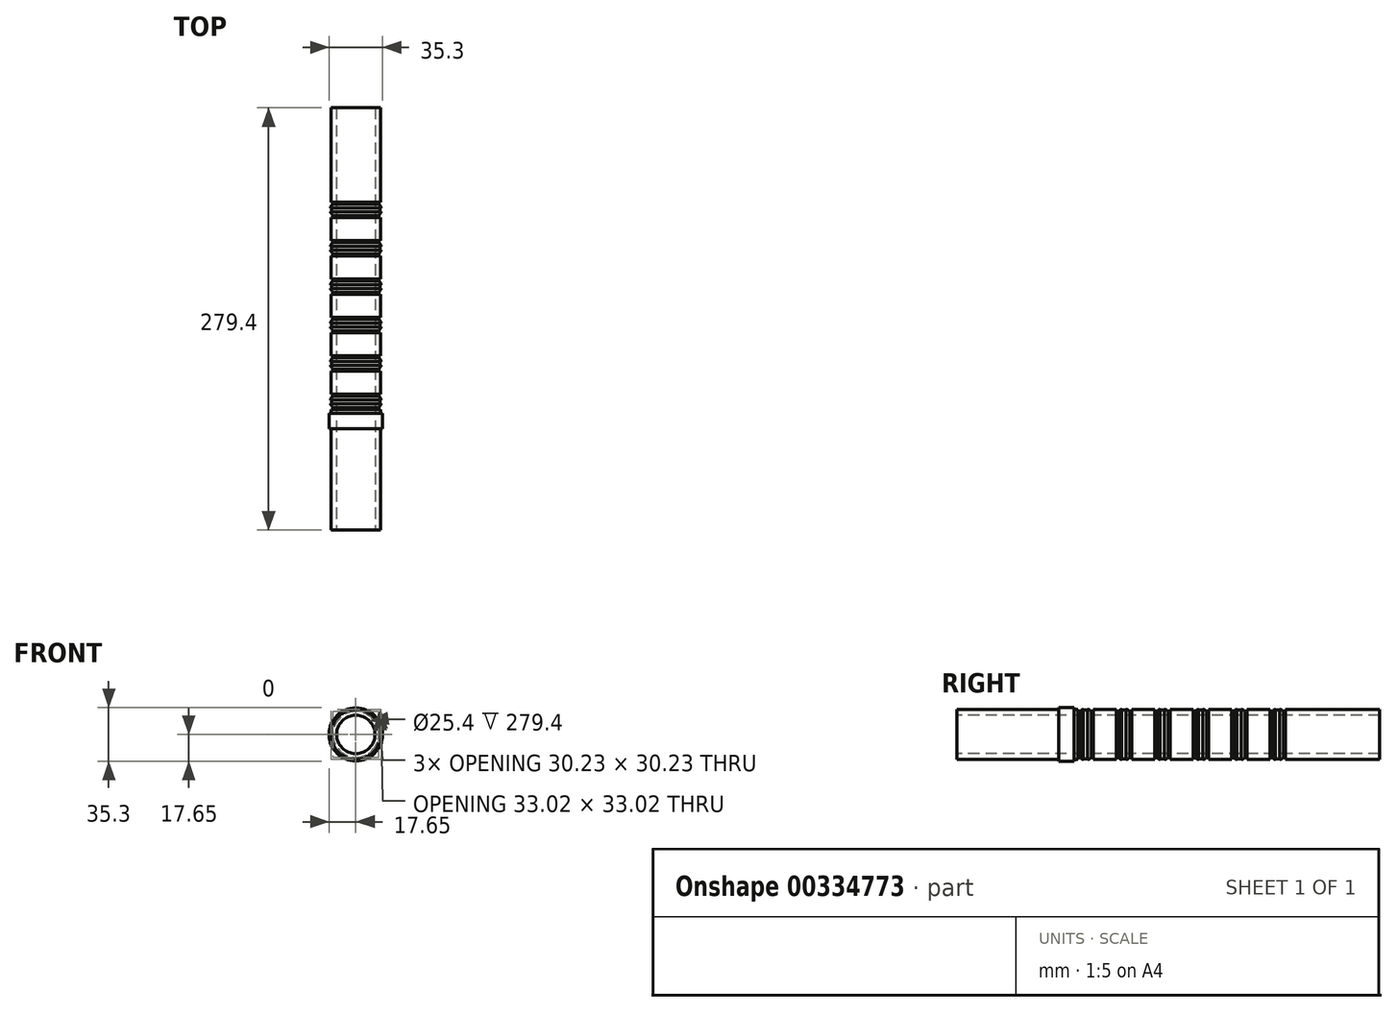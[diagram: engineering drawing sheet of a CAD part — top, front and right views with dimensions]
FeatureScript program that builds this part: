
annotation { "Feature Type Name" : "Feature", "Feature Type Description" : "" }
export const myFeature = defineFeature(function(context is Context, id is Id, definition is map)
    precondition{}
    {
        {
            var Q0;
            Q0=qCreatedBy(makeId("Front.planeOp"),FACE);
            var sketch = newSketch(context, id + "F0", { "sketchPlane" : qUnion([Q0])});
            skCircle(sketch, "E0", {"center": v(0, 0) * mm, "radius": 12.7 * mm});
            skCircle(sketch, "E1", {"center": v(0, 0) * mm, "radius": 16.51 * mm});
            skSolve(sketch);
        }
        {
            var Q0;
            Q0=makeQuery(id+"F0.imprint","IMPRINT",FACE,{"disambiguationData":[TD([[makeQuery(id+"F0.imprint","IMPRINT",EDGE,{"derivedFrom":sQuery(id+"F0.wireOp",EDGE,"E0")}),-1.0]])]});
            extrude(context, id + "F1", {"entities" : qUnion([Q0]), "oppositeDirection" : true, "depth" : 139.7 * mm, "hasSecondDirection" : true, "secondDirectionOppositeDirection" : false, "secondDirectionDepth" : 139.7 * mm});
        }
        {
            var Q0;
            Q0=qCreatedBy(makeId("Right.planeOp"),FACE);
            var sketch = newSketch(context, id + "F2", { "sketchPlane" : qUnion([Q0])});
            skLineSegment(sketch, "E2.bottom", {"start": v(-72.5, 17.65) * mm, "end": v(-62.33, 17.65) * mm});
            skLineSegment(sketch, "E2.top", {"start": v(-72.5, 15.11) * mm, "end": v(-62.33, 15.11) * mm});
            skLineSegment(sketch, "E2.left", {"start": v(-72.5, 17.65) * mm, "end": v(-72.5, 15.11) * mm});
            skLineSegment(sketch, "E2.right", {"start": v(-62.33, 17.65) * mm, "end": v(-62.33, 15.11) * mm});
            skLineSegment(sketch, "E3.1.0.0", {"start": v(-47.1, 17.65) * mm, "end": v(-36.93, 17.65) * mm});
            skLineSegment(sketch, "E3.1.0.1", {"start": v(-36.93, 17.65) * mm, "end": v(-36.93, 15.11) * mm});
            skLineSegment(sketch, "E3.1.0.2", {"start": v(-47.1, 15.11) * mm, "end": v(-36.93, 15.11) * mm});
            skLineSegment(sketch, "E3.1.0.3", {"start": v(-47.1, 17.65) * mm, "end": v(-47.1, 15.11) * mm});
            skLineSegment(sketch, "E3.2.0.0", {"start": v(-21.7, 17.65) * mm, "end": v(-11.53, 17.65) * mm});
            skLineSegment(sketch, "E3.2.0.1", {"start": v(-11.53, 17.65) * mm, "end": v(-11.53, 15.11) * mm});
            skLineSegment(sketch, "E3.2.0.2", {"start": v(-21.7, 15.11) * mm, "end": v(-11.53, 15.11) * mm});
            skLineSegment(sketch, "E3.2.0.3", {"start": v(-21.7, 17.65) * mm, "end": v(-21.7, 15.11) * mm});
            skLineSegment(sketch, "E4.1.0.0", {"start": v(3.7, 15.11) * mm, "end": v(13.87, 15.11) * mm});
            skLineSegment(sketch, "E4.1.0.1", {"start": v(13.87, 17.65) * mm, "end": v(13.87, 15.11) * mm});
            skLineSegment(sketch, "E4.1.0.2", {"start": v(3.7, 17.65) * mm, "end": v(3.7, 15.11) * mm});
            skLineSegment(sketch, "E4.1.0.4", {"start": v(29.1, 17.65) * mm, "end": v(39.27, 17.65) * mm});
            skLineSegment(sketch, "E4.1.0.5", {"start": v(29.1, 17.65) * mm, "end": v(29.1, 15.11) * mm});
            skLineSegment(sketch, "E4.1.0.6", {"start": v(29.1, 15.11) * mm, "end": v(39.27, 15.11) * mm});
            skLineSegment(sketch, "E4.1.0.7", {"start": v(39.27, 17.65) * mm, "end": v(39.27, 15.11) * mm});
            skLineSegment(sketch, "E4.1.0.8", {"start": v(54.5, 17.65) * mm, "end": v(54.5, 15.11) * mm});
            skLineSegment(sketch, "E4.1.0.9", {"start": v(54.5, 17.65) * mm, "end": v(64.67, 17.65) * mm});
            skLineSegment(sketch, "E4.1.0.10", {"start": v(54.5, 15.11) * mm, "end": v(64.67, 15.11) * mm});
            skLineSegment(sketch, "E4.1.0.11", {"start": v(64.67, 17.65) * mm, "end": v(64.67, 15.11) * mm});
            skLineSegment(sketch, "E4.2.0.0", {"start": v(79.9, 15.11) * mm, "end": v(90.07, 15.11) * mm});
            skLineSegment(sketch, "E4.2.0.1", {"start": v(90.07, 17.65) * mm, "end": v(90.07, 15.11) * mm});
            skLineSegment(sketch, "E4.2.0.2", {"start": v(79.9, 17.65) * mm, "end": v(79.9, 15.11) * mm});
            skLineSegment(sketch, "E5.trimOffspring", {"start": v(-21.7, 15.11) * mm, "end": v(-11.53, 15.11) * mm, "construction": true});
            skLineSegment(sketch, "E6.trimOffspring", {"start": v(-47.1, 15.11) * mm, "end": v(-36.93, 15.11) * mm, "construction": true});
            skLineSegment(sketch, "E7", {"start": v(3.7, 17.65) * mm, "end": v(13.87, 17.65) * mm});
            skLineSegment(sketch, "E8", {"start": v(79.9, 17.65) * mm, "end": v(90.07, 17.65) * mm});
            skLineSegment(sketch, "E9", {"start": v(-145.94, 0) * mm, "end": v(157.27, 0) * mm});
            skLineSegment(sketch, "E10.1.0.0", {"start": v(-49.63, 17.65) * mm, "end": v(-49.63, 15.11) * mm});
            skLineSegment(sketch, "E10.1.0.1", {"start": v(-59.8, 17.65) * mm, "end": v(-49.63, 17.65) * mm});
            skLineSegment(sketch, "E10.1.0.2", {"start": v(-59.8, 15.11) * mm, "end": v(-49.63, 15.11) * mm});
            skLineSegment(sketch, "E10.1.0.3", {"start": v(-59.8, 17.65) * mm, "end": v(-59.8, 15.11) * mm});
            skLineSegment(sketch, "E10.3.0.0", {"start": v(-24.23, 17.65) * mm, "end": v(-24.23, 15.11) * mm});
            skLineSegment(sketch, "E10.3.0.1", {"start": v(-34.4, 17.65) * mm, "end": v(-24.23, 17.65) * mm});
            skLineSegment(sketch, "E10.3.0.2", {"start": v(-34.4, 15.11) * mm, "end": v(-24.23, 15.11) * mm});
            skLineSegment(sketch, "E10.3.0.3", {"start": v(-34.4, 17.65) * mm, "end": v(-34.4, 15.11) * mm});
            skLineSegment(sketch, "E10.5.0.0", {"start": v(1.17, 17.65) * mm, "end": v(1.17, 15.11) * mm});
            skLineSegment(sketch, "E10.5.0.1", {"start": v(-9, 17.65) * mm, "end": v(1.17, 17.65) * mm});
            skLineSegment(sketch, "E10.5.0.2", {"start": v(-9, 15.11) * mm, "end": v(1.17, 15.11) * mm});
            skLineSegment(sketch, "E10.5.0.3", {"start": v(-9, 17.65) * mm, "end": v(-9, 15.11) * mm});
            skLineSegment(sketch, "E10.7.0.0", {"start": v(26.57, 17.65) * mm, "end": v(26.57, 15.11) * mm});
            skLineSegment(sketch, "E10.7.0.1", {"start": v(16.4, 17.65) * mm, "end": v(26.57, 17.65) * mm});
            skLineSegment(sketch, "E10.7.0.2", {"start": v(16.4, 15.11) * mm, "end": v(26.57, 15.11) * mm});
            skLineSegment(sketch, "E10.7.0.3", {"start": v(16.4, 17.65) * mm, "end": v(16.4, 15.11) * mm});
            skLineSegment(sketch, "E10.9.0.0", {"start": v(51.97, 17.65) * mm, "end": v(51.97, 15.11) * mm});
            skLineSegment(sketch, "E10.9.0.1", {"start": v(41.8, 17.65) * mm, "end": v(51.97, 17.65) * mm});
            skLineSegment(sketch, "E10.9.0.2", {"start": v(41.8, 15.11) * mm, "end": v(51.97, 15.11) * mm});
            skLineSegment(sketch, "E10.9.0.3", {"start": v(41.8, 17.65) * mm, "end": v(41.8, 15.11) * mm});
            skLineSegment(sketch, "E10.11.0.0", {"start": v(77.37, 17.65) * mm, "end": v(77.37, 15.11) * mm});
            skLineSegment(sketch, "E10.11.0.1", {"start": v(67.2, 17.65) * mm, "end": v(77.37, 17.65) * mm});
            skLineSegment(sketch, "E10.11.0.2", {"start": v(67.2, 15.11) * mm, "end": v(77.37, 15.11) * mm});
            skLineSegment(sketch, "E10.11.0.3", {"start": v(67.2, 17.65) * mm, "end": v(67.2, 15.11) * mm});
            skSolve(sketch);
        }
        {
            var Q0;
            Q0=makeQuery(id+"F2.imprint","IMPRINT",FACE,{"disambiguationData":[TD([[makeQuery(id+"F2.imprint","IMPRINT",EDGE,{"derivedFrom":sQuery(id+"F2.wireOp",EDGE,"E10.1.0.0")}),-1.0]])]});
            var Q1;
            Q1=makeQuery(id+"F2.imprint","IMPRINT",FACE,{"disambiguationData":[TD([[makeQuery(id+"F2.imprint","IMPRINT",EDGE,{"derivedFrom":sQuery(id+"F2.wireOp",EDGE,"E10.3.0.0")}),-1.0]])]});
            var Q2;
            Q2=makeQuery(id+"F2.imprint","IMPRINT",FACE,{"disambiguationData":[TD([[makeQuery(id+"F2.imprint","IMPRINT",EDGE,{"derivedFrom":sQuery(id+"F2.wireOp",EDGE,"E10.5.0.0")}),-1.0]])]});
            var Q3;
            Q3=makeQuery(id+"F2.imprint","IMPRINT",FACE,{"disambiguationData":[TD([[makeQuery(id+"F2.imprint","IMPRINT",EDGE,{"derivedFrom":sQuery(id+"F2.wireOp",EDGE,"E10.7.0.0")}),-1.0]])]});
            var Q4;
            Q4=makeQuery(id+"F2.imprint","IMPRINT",FACE,{"disambiguationData":[TD([[makeQuery(id+"F2.imprint","IMPRINT",EDGE,{"derivedFrom":sQuery(id+"F2.wireOp",EDGE,"E10.9.0.0")}),-1.0]])]});
            var Q5;
            Q5=makeQuery(id+"F2.imprint","IMPRINT",FACE,{"disambiguationData":[TD([[makeQuery(id+"F2.imprint","IMPRINT",EDGE,{"derivedFrom":sQuery(id+"F2.wireOp",EDGE,"E10.11.0.0")}),-1.0]])]});
            var Q6;
            Q6=sQuery(id+"F2.wireOp",EDGE,"E9");
            revolve(context, id + "F3", {"operationType" : NewBodyOperationType.REMOVE, "entities" : qUnion([Q0, Q1, Q2, Q3, Q4, Q5]), "axis" : qUnion([Q6]), "revolveType" : RevolveType.FULL, "oppositeDirection" : true});
        }
        {
            var Q0;
            Q0=makeQuery(id+"F2.imprint","IMPRINT",FACE,{"disambiguationData":[TD([[makeQuery(id+"F2.imprint","IMPRINT",EDGE,{"derivedFrom":sQuery(id+"F2.wireOp",EDGE,"E2.bottom")}),-1.0]])]});
            var Q1;
            Q1=makeQuery(id+"F2.imprint","IMPRINT",FACE,{"disambiguationData":[TD([[makeQuery(id+"F2.imprint","IMPRINT",EDGE,{"derivedFrom":sQuery(id+"F2.wireOp",EDGE,"E3.1.0.1")}),-1.0]])]});
            var Q2;
            Q2=makeQuery(id+"F2.imprint","IMPRINT",FACE,{"disambiguationData":[TD([[makeQuery(id+"F2.imprint","IMPRINT",EDGE,{"derivedFrom":sQuery(id+"F2.wireOp",EDGE,"E3.2.0.1")}),-1.0]])]});
            var Q3;
            Q3=makeQuery(id+"F2.imprint","IMPRINT",FACE,{"disambiguationData":[TD([[makeQuery(id+"F2.imprint","IMPRINT",EDGE,{"derivedFrom":sQuery(id+"F2.wireOp",EDGE,"E4.1.0.1")}),-1.0]])]});
            var Q4;
            Q4=makeQuery(id+"F2.imprint","IMPRINT",FACE,{"disambiguationData":[TD([[makeQuery(id+"F2.imprint","IMPRINT",EDGE,{"derivedFrom":sQuery(id+"F2.wireOp",EDGE,"E4.1.0.7")}),-1.0]])]});
            var Q5;
            Q5=makeQuery(id+"F2.imprint","IMPRINT",FACE,{"disambiguationData":[TD([[makeQuery(id+"F2.imprint","IMPRINT",EDGE,{"derivedFrom":sQuery(id+"F2.wireOp",EDGE,"E4.1.0.11")}),-1.0]])]});
            var Q6;
            Q6=makeQuery(id+"F2.imprint","IMPRINT",FACE,{"disambiguationData":[TD([[makeQuery(id+"F2.imprint","IMPRINT",EDGE,{"derivedFrom":sQuery(id+"F2.wireOp",EDGE,"E4.2.0.1")}),-1.0]])]});
            var Q7;
            Q7=sQuery(id+"F2.wireOp",EDGE,"E9");
            revolve(context, id + "F4", {"operationType" : NewBodyOperationType.ADD, "entities" : qUnion([Q0, Q1, Q2, Q3, Q4, Q5, Q6]), "axis" : qUnion([Q7]), "revolveType" : RevolveType.FULL});
        }
        {
            var Q0;
            Q0=qCreatedBy(makeId("Right.planeOp"),FACE);
            var sketch = newSketch(context, id + "F5", { "sketchPlane" : qUnion([Q0])});
            skArc(sketch, "E11", {"start": v(-50.9, 15.16) * mm, "mid": v(-52.09, 16.15) * mm, "end": v(-53.51, 16.74) * mm});
            skLineSegment(sketch, "E12", {"start": v(-58.52, 15.16) * mm, "end": v(-58.52, 14.73) * mm});
            skLineSegment(sketch, "E13", {"start": v(-58.52, 14.73) * mm, "end": v(-50.9, 14.73) * mm});
            skLineSegment(sketch, "E14", {"start": v(-50.9, 14.73) * mm, "end": v(-50.9, 15.16) * mm});
            skArc(sketch, "E15.1.0.0", {"start": v(-25.5, 15.16) * mm, "mid": v(-26.69, 16.15) * mm, "end": v(-28.11, 16.74) * mm});
            skLineSegment(sketch, "E15.1.0.1", {"start": v(-33.12, 15.16) * mm, "end": v(-33.12, 14.73) * mm});
            skLineSegment(sketch, "E15.1.0.2", {"start": v(-33.12, 14.73) * mm, "end": v(-25.5, 14.73) * mm});
            skLineSegment(sketch, "E15.1.0.3", {"start": v(-25.5, 14.73) * mm, "end": v(-25.5, 15.16) * mm});
            skArc(sketch, "E15.2.0.0", {"start": v(-0.1, 15.16) * mm, "mid": v(-1.29, 16.15) * mm, "end": v(-2.71, 16.74) * mm});
            skLineSegment(sketch, "E15.2.0.1", {"start": v(-7.72, 15.16) * mm, "end": v(-7.72, 14.73) * mm});
            skLineSegment(sketch, "E15.2.0.2", {"start": v(-7.72, 14.73) * mm, "end": v(-0.1, 14.73) * mm});
            skLineSegment(sketch, "E15.2.0.3", {"start": v(-0.1, 14.73) * mm, "end": v(-0.1, 15.16) * mm});
            skArc(sketch, "E15.3.0.0", {"start": v(25.3, 15.16) * mm, "mid": v(24.11, 16.15) * mm, "end": v(22.69, 16.74) * mm});
            skLineSegment(sketch, "E15.3.0.1", {"start": v(17.68, 15.16) * mm, "end": v(17.68, 14.73) * mm});
            skLineSegment(sketch, "E15.3.0.2", {"start": v(17.68, 14.73) * mm, "end": v(25.3, 14.73) * mm});
            skLineSegment(sketch, "E15.3.0.3", {"start": v(25.3, 14.73) * mm, "end": v(25.3, 15.16) * mm});
            skArc(sketch, "E15.4.0.0", {"start": v(50.7, 15.16) * mm, "mid": v(49.51, 16.15) * mm, "end": v(48.09, 16.74) * mm});
            skLineSegment(sketch, "E15.4.0.1", {"start": v(43.08, 15.16) * mm, "end": v(43.08, 14.73) * mm});
            skLineSegment(sketch, "E15.4.0.2", {"start": v(43.08, 14.73) * mm, "end": v(50.7, 14.73) * mm});
            skLineSegment(sketch, "E15.4.0.3", {"start": v(50.7, 14.73) * mm, "end": v(50.7, 15.16) * mm});
            skArc(sketch, "E15.5.0.0", {"start": v(76.1, 15.16) * mm, "mid": v(74.91, 16.15) * mm, "end": v(73.49, 16.74) * mm});
            skLineSegment(sketch, "E15.5.0.1", {"start": v(68.48, 15.16) * mm, "end": v(68.48, 14.73) * mm});
            skLineSegment(sketch, "E15.5.0.2", {"start": v(68.48, 14.73) * mm, "end": v(76.1, 14.73) * mm});
            skLineSegment(sketch, "E15.5.0.3", {"start": v(76.1, 14.73) * mm, "end": v(76.1, 15.16) * mm});
            skLineSegment(sketch, "E16", {"start": v(-83.04, 0) * mm, "end": v(106.72, 0) * mm});
            skLineSegment(sketch, "E17.top", {"start": v(-53.51, 16.06) * mm, "end": v(-56.12, 16.06) * mm});
            skLineSegment(sketch, "E17.left", {"start": v(-53.51, 16.74) * mm, "end": v(-53.51, 16.06) * mm});
            skLineSegment(sketch, "E17.right", {"start": v(-56.12, 16.68) * mm, "end": v(-56.12, 16.06) * mm});
            skPoint(sketch, "E17.middle", {"position": v(-54.82, 16.88) * mm});
            skArc(sketch, "E18.trimOffspring", {"start": v(-56.12, 16.68) * mm, "mid": v(-57.43, 16.1) * mm, "end": v(-58.52, 15.16) * mm});
            skPoint(sketch, "E19.orphan", {"position": v(-56.12, 17.7) * mm});
            skPoint(sketch, "E20.orphan", {"position": v(-53.51, 17.7) * mm});
            skLineSegment(sketch, "E21.1.0.0", {"start": v(-28.11, 16.74) * mm, "end": v(-28.11, 16.06) * mm});
            skLineSegment(sketch, "E21.1.0.1", {"start": v(-30.72, 16.68) * mm, "end": v(-30.72, 16.06) * mm});
            skLineSegment(sketch, "E21.1.0.2", {"start": v(-28.11, 16.06) * mm, "end": v(-30.72, 16.06) * mm});
            skLineSegment(sketch, "E21.2.0.0", {"start": v(-2.71, 16.74) * mm, "end": v(-2.71, 16.06) * mm});
            skLineSegment(sketch, "E21.2.0.1", {"start": v(-5.32, 16.68) * mm, "end": v(-5.32, 16.06) * mm});
            skLineSegment(sketch, "E21.2.0.2", {"start": v(-2.71, 16.06) * mm, "end": v(-5.32, 16.06) * mm});
            skLineSegment(sketch, "E21.3.0.0", {"start": v(22.69, 16.74) * mm, "end": v(22.69, 16.06) * mm});
            skLineSegment(sketch, "E21.3.0.1", {"start": v(20.08, 16.68) * mm, "end": v(20.08, 16.06) * mm});
            skLineSegment(sketch, "E21.3.0.2", {"start": v(22.69, 16.06) * mm, "end": v(20.08, 16.06) * mm});
            skLineSegment(sketch, "E21.4.0.0", {"start": v(48.09, 16.74) * mm, "end": v(48.09, 16.06) * mm});
            skLineSegment(sketch, "E21.4.0.1", {"start": v(45.48, 16.68) * mm, "end": v(45.48, 16.06) * mm});
            skLineSegment(sketch, "E21.4.0.2", {"start": v(48.09, 16.06) * mm, "end": v(45.48, 16.06) * mm});
            skLineSegment(sketch, "E21.5.0.0", {"start": v(73.49, 16.74) * mm, "end": v(73.49, 16.06) * mm});
            skLineSegment(sketch, "E21.5.0.1", {"start": v(70.88, 16.68) * mm, "end": v(70.88, 16.06) * mm});
            skLineSegment(sketch, "E21.5.0.2", {"start": v(73.49, 16.06) * mm, "end": v(70.88, 16.06) * mm});
            skArc(sketch, "E22.trimOffspring", {"start": v(-30.72, 16.68) * mm, "mid": v(-32.03, 16.1) * mm, "end": v(-33.12, 15.16) * mm});
            skLineSegment(sketch, "E23.trimOffspring", {"start": v(-30.72, 16.06) * mm, "end": v(-28.11, 16.06) * mm, "construction": true});
            skArc(sketch, "E24.trimOffspring", {"start": v(-5.32, 16.68) * mm, "mid": v(-6.63, 16.1) * mm, "end": v(-7.72, 15.16) * mm});
            skArc(sketch, "E25.trimOffspring", {"start": v(20.08, 16.68) * mm, "mid": v(18.77, 16.1) * mm, "end": v(17.68, 15.16) * mm});
            skArc(sketch, "E26.trimOffspring", {"start": v(45.48, 16.68) * mm, "mid": v(44.17, 16.1) * mm, "end": v(43.08, 15.16) * mm});
            skArc(sketch, "E27.trimOffspring", {"start": v(70.88, 16.68) * mm, "mid": v(69.57, 16.1) * mm, "end": v(68.48, 15.16) * mm});
            skSolve(sketch);
        }
        {
            var Q0;
            Q0=makeQuery(id+"F5.imprint","IMPRINT",FACE,{"disambiguationData":[TD([[makeQuery(id+"F5.imprint","IMPRINT",EDGE,{"derivedFrom":sQuery(id+"F5.wireOp",EDGE,"E11")}),1.0]])]});
            var Q1;
            Q1=makeQuery(id+"F5.imprint","IMPRINT",FACE,{"disambiguationData":[TD([[makeQuery(id+"F5.imprint","IMPRINT",EDGE,{"derivedFrom":sQuery(id+"F5.wireOp",EDGE,"E15.1.0.0")}),1.0]])]});
            var Q2;
            Q2=makeQuery(id+"F5.imprint","IMPRINT",FACE,{"disambiguationData":[TD([[makeQuery(id+"F5.imprint","IMPRINT",EDGE,{"derivedFrom":sQuery(id+"F5.wireOp",EDGE,"E15.2.0.0")}),1.0]])]});
            var Q3;
            Q3=makeQuery(id+"F5.imprint","IMPRINT",FACE,{"disambiguationData":[TD([[makeQuery(id+"F5.imprint","IMPRINT",EDGE,{"derivedFrom":sQuery(id+"F5.wireOp",EDGE,"E15.3.0.0")}),1.0]])]});
            var Q4;
            Q4=makeQuery(id+"F5.imprint","IMPRINT",FACE,{"disambiguationData":[TD([[makeQuery(id+"F5.imprint","IMPRINT",EDGE,{"derivedFrom":sQuery(id+"F5.wireOp",EDGE,"E15.4.0.0")}),1.0]])]});
            var Q5;
            Q5=makeQuery(id+"F5.imprint","IMPRINT",FACE,{"disambiguationData":[TD([[makeQuery(id+"F5.imprint","IMPRINT",EDGE,{"derivedFrom":sQuery(id+"F5.wireOp",EDGE,"E15.5.0.0")}),1.0]])]});
            var Q6;
            Q6=sQuery(id+"F5.wireOp",EDGE,"E16");
            revolve(context, id + "F6", {"operationType" : NewBodyOperationType.ADD, "entities" : qUnion([Q0, Q1, Q2, Q3, Q4, Q5]), "axis" : qUnion([Q6]), "revolveType" : RevolveType.FULL});
        }
    });
